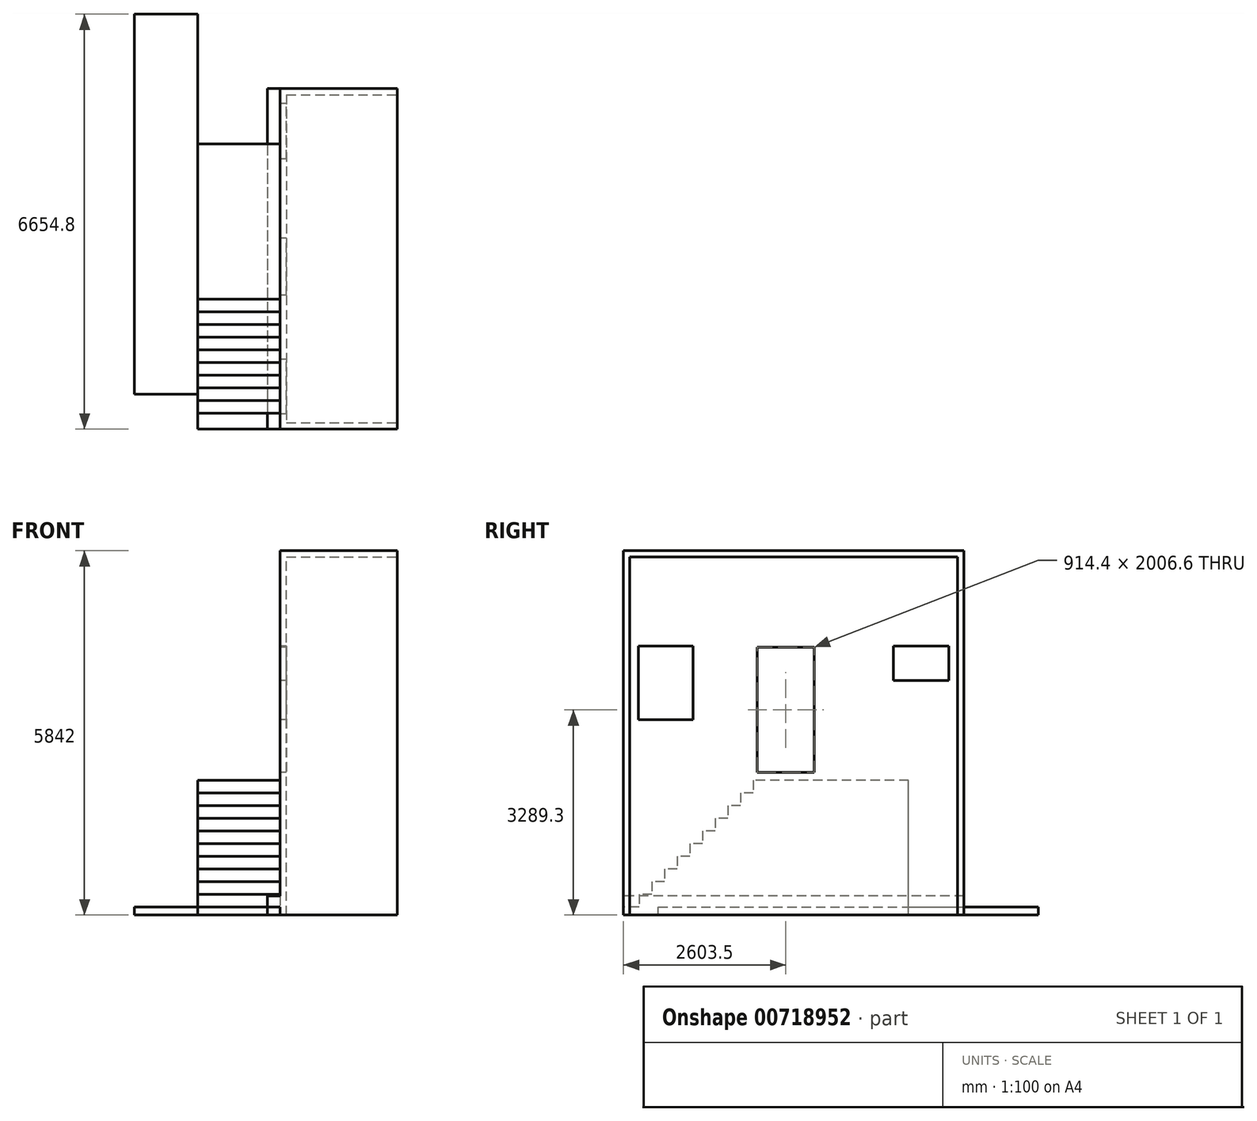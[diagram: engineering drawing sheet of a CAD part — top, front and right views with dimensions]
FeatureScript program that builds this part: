
annotation { "Feature Type Name" : "Feature", "Feature Type Description" : "" }
export const myFeature = defineFeature(function(context is Context, id is Id, definition is map)
    precondition{}
    {
        {
            var Q0;
            Q0=qCreatedBy(makeId("Front.planeOp"),FACE);
            var sketch = newSketch(context, id + "F0", { "sketchPlane" : qUnion([Q0])});
            skLineSegment(sketch, "E0.bottom", {"start": v(0, 0) * mm, "end": v(1879.6, 0) * mm});
            skLineSegment(sketch, "E0.top", {"start": v(0, 5842) * mm, "end": v(1879.6, 5842) * mm});
            skLineSegment(sketch, "E0.left", {"start": v(0, 304.8) * mm, "end": v(0, 5842) * mm});
            skLineSegment(sketch, "E0.right", {"start": v(1879.6, 0) * mm, "end": v(1879.6, 5842) * mm});
            skLineSegment(sketch, "E1.bottom", {"start": v(0, 0) * mm, "end": v(-203.2, 0) * mm});
            skLineSegment(sketch, "E1.top", {"start": v(0, 304.8) * mm, "end": v(-203.2, 304.8) * mm});
            skLineSegment(sketch, "E1.right", {"start": v(-203.2, 0) * mm, "end": v(-203.2, 304.8) * mm});
            skSolve(sketch);
        }
        {
            var Q0;
            Q0 = qSketchRegion(id + "F0", true);
            extrude(context, id + "F1", {"entities" : qUnion([Q0]), "oppositeDirection" : true, "depth" : 5461 * mm, "offsetDistance" : 25.4 * mm});
        }
        {
            var Q0;
            Q0=makeQuery(id+"F1.opExtrude","SWEPT_FACE",FACE,{"disambiguationData":[OSD([sQuery(id+"F0.wireOp",EDGE,"E0.left")])]});
            var sketch = newSketch(context, id + "F2", { "sketchPlane" : qUnion([Q0])});
            skLineSegment(sketch, "E2.bottom", {"start": v(-5219.7, 3759.2) * mm, "end": v(-4330.7, 3759.2) * mm});
            skLineSegment(sketch, "E2.top", {"start": v(-5219.7, 4311.65) * mm, "end": v(-4330.7, 4311.65) * mm});
            skLineSegment(sketch, "E2.left", {"start": v(-5219.7, 3759.2) * mm, "end": v(-5219.7, 4311.65) * mm});
            skLineSegment(sketch, "E2.right", {"start": v(-4330.7, 3759.2) * mm, "end": v(-4330.7, 4311.65) * mm});
            skLineSegment(sketch, "E3.bottom", {"start": v(-3060.7, 2286) * mm, "end": v(-2146.3, 2286) * mm});
            skLineSegment(sketch, "E3.top", {"start": v(-3060.7, 4292.6) * mm, "end": v(-2146.3, 4292.6) * mm});
            skLineSegment(sketch, "E3.left", {"start": v(-3060.7, 2286) * mm, "end": v(-3060.7, 4292.6) * mm});
            skLineSegment(sketch, "E3.right", {"start": v(-2146.3, 2286) * mm, "end": v(-2146.3, 4292.6) * mm});
            skLineSegment(sketch, "E4.bottom", {"start": v(-1117.6, 4311.65) * mm, "end": v(-241.3, 4311.65) * mm});
            skLineSegment(sketch, "E4.top", {"start": v(-1117.6, 3130.55) * mm, "end": v(-241.3, 3130.55) * mm});
            skLineSegment(sketch, "E4.left", {"start": v(-1117.6, 4311.65) * mm, "end": v(-1117.6, 3130.55) * mm});
            skLineSegment(sketch, "E4.right", {"start": v(-241.3, 4311.65) * mm, "end": v(-241.3, 3130.55) * mm});
            skSolve(sketch);
        }
        {
            var Q0;
            Q0=makeQuery(id+"F1.opExtrude","SWEPT_FACE",FACE,{"disambiguationData":[OSD([sQuery(id+"F0.wireOp",EDGE,"E0.right")])]});
            var sketch = newSketch(context, id + "F3", { "sketchPlane" : qUnion([Q0])});
            skLineSegment(sketch, "E5.bottom", {"start": v(101.6, 0) * mm, "end": v(5359.4, 0) * mm});
            skLineSegment(sketch, "E5.top", {"start": v(101.6, 5740.4) * mm, "end": v(5359.4, 5740.4) * mm});
            skLineSegment(sketch, "E5.left", {"start": v(101.6, 0) * mm, "end": v(101.6, 5740.4) * mm});
            skLineSegment(sketch, "E5.right", {"start": v(5359.4, 0) * mm, "end": v(5359.4, 5740.4) * mm});
            skSolve(sketch);
        }
        {
            var Q0;
            Q0=makeQuery(id+"F3.imprint","IMPRINT",FACE,{"disambiguationData":[TD([[makeQuery(id+"F3.imprint","IMPRINT",EDGE,{"derivedFrom":sQuery(id+"F3.wireOp",EDGE,"E5.bottom")}),-1.0]])]});
            extrude(context, id + "F4", {"entities" : qUnion([Q0]), "operationType" : NewBodyOperationType.REMOVE, "oppositeDirection" : true, "depth" : 1778 * mm, "offsetDistance" : 25.4 * mm});
        }
        {
            var Q0;
            Q0=makeQuery(id+"F2.imprint","IMPRINT",FACE,{"disambiguationData":[TD([[makeQuery(id+"F2.imprint","IMPRINT",EDGE,{"derivedFrom":sQuery(id+"F2.wireOp",EDGE,"E2.bottom")}),1.0]])]});
            var Q1;
            Q1=makeQuery(id+"F2.imprint","IMPRINT",FACE,{"disambiguationData":[TD([[makeQuery(id+"F2.imprint","IMPRINT",EDGE,{"derivedFrom":sQuery(id+"F2.wireOp",EDGE,"E3.bottom")}),1.0]])]});
            var Q2;
            Q2=makeQuery(id+"F2.imprint","IMPRINT",FACE,{"disambiguationData":[TD([[makeQuery(id+"F2.imprint","IMPRINT",EDGE,{"derivedFrom":sQuery(id+"F2.wireOp",EDGE,"E4.bottom")}),-1.0]])]});
            extrude(context, id + "F5", {"entities" : qUnion([Q0, Q1, Q2]), "operationType" : NewBodyOperationType.REMOVE, "endBound" : BoundingType.THROUGH_ALL, "oppositeDirection" : true, "depth" : 25.4 * mm, "offsetDistance" : 25.4 * mm});
        }
        {
            var Q0;
            Q0=makeQuery(id+"F2.imprint","IMPRINT",FACE,{"disambiguationData":[TD([[makeQuery(id+"F2.imprint","IMPRINT",EDGE,{"derivedFrom":sQuery(id+"F2.wireOp",EDGE,"E2.bottom")}),-1.0]])]});
            var sketch = newSketch(context, id + "F6", { "sketchPlane" : qUnion([Q0])});
            skLineSegment(sketch, "E6", {"start": v(-4572, 304.8) * mm, "end": v(-4572, 2159) * mm});
            skLineSegment(sketch, "E7", {"start": v(-4572, 2159) * mm, "end": v(-2082.8, 2159) * mm});
            skLineSegment(sketch, "E8", {"start": v(-2082.8, 2159) * mm, "end": v(-2082.8, 1955.8) * mm});
            skLineSegment(sketch, "E9", {"start": v(-2082.8, 1955.8) * mm, "end": v(-1879.6, 1955.8) * mm});
            skLineSegment(sketch, "E10", {"start": v(-1879.6, 1955.8) * mm, "end": v(-1879.6, 1752.6) * mm});
            skLineSegment(sketch, "E11", {"start": v(-1879.6, 1752.6) * mm, "end": v(-1676.4, 1752.6) * mm});
            skLineSegment(sketch, "E12", {"start": v(-1676.4, 1752.6) * mm, "end": v(-1676.4, 1549.4) * mm});
            skLineSegment(sketch, "E13", {"start": v(-1676.4, 1549.4) * mm, "end": v(-1473.2, 1549.4) * mm});
            skLineSegment(sketch, "E14", {"start": v(-1473.2, 1549.4) * mm, "end": v(-1473.2, 1346.2) * mm});
            skLineSegment(sketch, "E15", {"start": v(-1473.2, 1346.2) * mm, "end": v(-1270, 1346.2) * mm});
            skLineSegment(sketch, "E16", {"start": v(-1270, 1346.2) * mm, "end": v(-1270, 1143) * mm});
            skLineSegment(sketch, "E17", {"start": v(-1270, 1143) * mm, "end": v(-1066.8, 1143) * mm});
            skLineSegment(sketch, "E18", {"start": v(-1066.8, 1143) * mm, "end": v(-1066.8, 939.8) * mm});
            skLineSegment(sketch, "E19", {"start": v(-1066.8, 939.8) * mm, "end": v(-863.6, 939.8) * mm});
            skLineSegment(sketch, "E20", {"start": v(-863.6, 939.8) * mm, "end": v(-863.6, 736.6) * mm});
            skLineSegment(sketch, "E21", {"start": v(-863.6, 736.6) * mm, "end": v(-660.4, 736.6) * mm});
            skLineSegment(sketch, "E22", {"start": v(-660.4, 736.6) * mm, "end": v(-660.4, 533.4) * mm});
            skLineSegment(sketch, "E23", {"start": v(-660.4, 533.4) * mm, "end": v(-457.2, 533.4) * mm});
            skLineSegment(sketch, "E24", {"start": v(-457.2, 533.4) * mm, "end": v(-457.2, 330.2) * mm});
            skLineSegment(sketch, "E25", {"start": v(-457.2, 330.2) * mm, "end": v(-254, 330.2) * mm});
            skLineSegment(sketch, "E26", {"start": v(-254, 330.2) * mm, "end": v(-254, 127) * mm});
            skLineSegment(sketch, "E27", {"start": v(-254, 127) * mm, "end": v(0, 127) * mm});
            skLineSegment(sketch, "E28", {"start": v(0, 127) * mm, "end": v(0, 0) * mm});
            skLineSegment(sketch, "E29", {"start": v(0, 0) * mm, "end": v(-4572, 0) * mm});
            skLineSegment(sketch, "E30", {"start": v(-4572, 0) * mm, "end": v(-4572, 304.8) * mm});
            skSolve(sketch);
        }
        {
            var Q0;
            Q0 = qSketchRegion(id + "F6", true);
            extrude(context, id + "F7", {"entities" : qUnion([Q0]), "depth" : 1320.8 * mm, "offsetDistance" : 25.4 * mm});
        }
        {
            var Q0;
            Q0=makeQuery(id+"F7.opExtrude","CAP_FACE",FACE,{"disambiguationData":[OSD([sQuery(id+"F6.wireOp",EDGE,"E6"),sQuery(id+"F6.wireOp",EDGE,"E7"),sQuery(id+"F6.wireOp",EDGE,"E8"),sQuery(id+"F6.wireOp",EDGE,"E9"),sQuery(id+"F6.wireOp",EDGE,"E10"),sQuery(id+"F6.wireOp",EDGE,"E11"),sQuery(id+"F6.wireOp",EDGE,"E12"),sQuery(id+"F6.wireOp",EDGE,"E13"),sQuery(id+"F6.wireOp",EDGE,"E14"),sQuery(id+"F6.wireOp",EDGE,"E15"),sQuery(id+"F6.wireOp",EDGE,"E16"),sQuery(id+"F6.wireOp",EDGE,"E17"),sQuery(id+"F6.wireOp",EDGE,"E18"),sQuery(id+"F6.wireOp",EDGE,"E19"),sQuery(id+"F6.wireOp",EDGE,"E20"),sQuery(id+"F6.wireOp",EDGE,"E21"),sQuery(id+"F6.wireOp",EDGE,"E22"),sQuery(id+"F6.wireOp",EDGE,"E23"),sQuery(id+"F6.wireOp",EDGE,"E24"),sQuery(id+"F6.wireOp",EDGE,"E25"),sQuery(id+"F6.wireOp",EDGE,"E26"),sQuery(id+"F6.wireOp",EDGE,"E27"),sQuery(id+"F6.wireOp",EDGE,"E28"),sQuery(id+"F6.wireOp",EDGE,"E29"),sQuery(id+"F6.wireOp",EDGE,"E30")])],"isStart":false});
            var sketch = newSketch(context, id + "F8", { "sketchPlane" : qUnion([Q0])});
            skLineSegment(sketch, "E31.bottom", {"start": v(-558.8, 0) * mm, "end": v(-6654.8, 0) * mm});
            skLineSegment(sketch, "E31.top", {"start": v(-558.8, 127) * mm, "end": v(-6654.8, 127) * mm});
            skLineSegment(sketch, "E31.left", {"start": v(-558.8, 0) * mm, "end": v(-558.8, 127) * mm});
            skLineSegment(sketch, "E31.right", {"start": v(-6654.8, 0) * mm, "end": v(-6654.8, 127) * mm});
            skSolve(sketch);
        }
        {
            var Q0;
            Q0 = qSketchRegion(id + "F8", true);
            extrude(context, id + "F9", {"entities" : qUnion([Q0]), "operationType" : NewBodyOperationType.ADD, "depth" : 1016 * mm, "offsetDistance" : 25.4 * mm});
        }
    });
